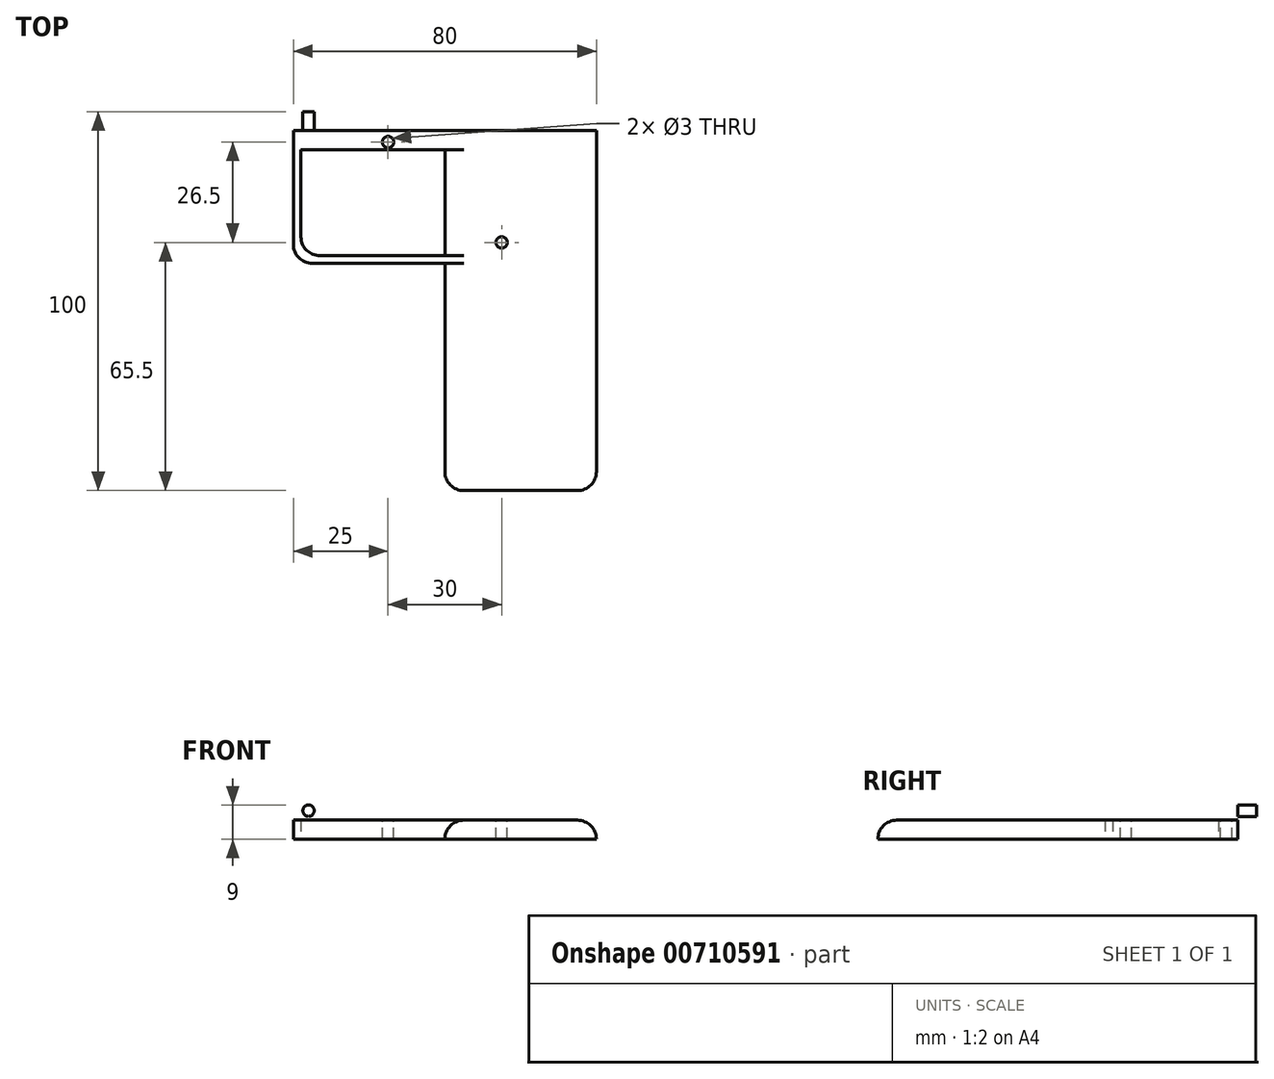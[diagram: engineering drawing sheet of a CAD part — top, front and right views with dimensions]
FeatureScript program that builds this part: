
annotation { "Feature Type Name" : "Feature", "Feature Type Description" : "" }
export const myFeature = defineFeature(function(context is Context, id is Id, definition is map)
    precondition{}
    {
        {
            var Q0;
            Q0=qCreatedBy(makeId("Top.planeOp"),FACE);
            var sketch = newSketch(context, id + "F0", { "sketchPlane" : qUnion([Q0])});
            skLineSegment(sketch, "E0.bottom", {"start": v(20, 50) * mm, "end": v(-20, 50) * mm});
            skLineSegment(sketch, "E0.top", {"start": v(20, -50) * mm, "end": v(-20, -50) * mm});
            skLineSegment(sketch, "E0.left", {"start": v(20, 50) * mm, "end": v(20, -50) * mm});
            skLineSegment(sketch, "E0.right", {"start": v(-20, 50) * mm, "end": v(-20, -50) * mm});
            skPoint(sketch, "E0.middle", {"position": v(0, 0) * mm});
            skLineSegment(sketch, "E1.bottom", {"start": v(-20, 50) * mm, "end": v(-60, 50) * mm});
            skLineSegment(sketch, "E1.top", {"start": v(-20, 10) * mm, "end": v(-60, 10) * mm});
            skLineSegment(sketch, "E1.left", {"start": v(-20, 50) * mm, "end": v(-20, 10) * mm});
            skLineSegment(sketch, "E1.right", {"start": v(-60, 50) * mm, "end": v(-60, 10) * mm});
            skLineSegment(sketch, "E2", {"start": v(-60, 50) * mm, "end": v(-58, 50) * mm});
            skLineSegment(sketch, "E3", {"start": v(-58, 50) * mm, "end": v(-58, 40) * mm});
            skLineSegment(sketch, "E4", {"start": v(-20, 10) * mm, "end": v(-20, 12) * mm});
            skLineSegment(sketch, "E5.bottom", {"start": v(-20, 12) * mm, "end": v(-58, 12) * mm});
            skLineSegment(sketch, "E5.top", {"start": v(-20, 40) * mm, "end": v(-58, 40) * mm});
            skLineSegment(sketch, "E5.left", {"start": v(-20, 12) * mm, "end": v(-20, 40) * mm});
            skLineSegment(sketch, "E5.right", {"start": v(-58, 12) * mm, "end": v(-58, 40) * mm});
            skSolve(sketch);
        }
        {
            var Q0;
            Q0=makeQuery(id+"F0.imprint","IMPRINT",FACE,{"disambiguationData":[TD([[makeQuery(id+"F0.imprint","IMPRINT",EDGE,{"derivedFrom":sQuery(id+"F0.wireOp",EDGE,"E0.bottom")}),1.0]])]});
            var Q1;
            Q1=makeQuery(id+"F0.imprint","IMPRINT",FACE,{"disambiguationData":[TD([[makeQuery(id+"F0.imprint","IMPRINT",EDGE,{"derivedFrom":sQuery(id+"F0.wireOp",EDGE,"E1.bottom")}),1.0]])]});
            var Q2;
            Q2=makeQuery(id+"F0.imprint","IMPRINT",FACE,{"disambiguationData":[TD([[makeQuery(id+"F0.imprint","IMPRINT",EDGE,{"derivedFrom":sQuery(id+"F0.wireOp",EDGE,"E1.top")}),-1.0]])]});
            extrude(context, id + "F1", {"entities" : qUnion([Q0, Q1, Q2]), "depth" : 5 * mm, "offsetDistance" : 25 * mm});
        }
        {
            var Q0;
            Q0=makeQuery(id+"F1.opExtrude","CAP_FACE",FACE,{"disambiguationData":[OSD([sQuery(id+"F0.wireOp",EDGE,"E0.bottom"),sQuery(id+"F0.wireOp",EDGE,"E0.top"),sQuery(id+"F0.wireOp",EDGE,"E0.left"),sQuery(id+"F0.wireOp",EDGE,"E0.right"),sQuery(id+"F0.wireOp",EDGE,"E1.bottom"),sQuery(id+"F0.wireOp",EDGE,"E1.top"),sQuery(id+"F0.wireOp",EDGE,"E1.right"),sQuery(id+"F0.wireOp",EDGE,"E2"),sQuery(id+"F0.wireOp",EDGE,"E5.bottom"),sQuery(id+"F0.wireOp",EDGE,"E5.top"),sQuery(id+"F0.wireOp",EDGE,"E5.left"),sQuery(id+"F0.wireOp",EDGE,"E5.right")])],"isStart":false});
            var sketch = newSketch(context, id + "F2", { "sketchPlane" : qUnion([Q0])});
            skLineSegment(sketch, "E6", {"start": v(-20, 40) * mm, "end": v(-35, 40) * mm, "construction": true});
            skLineSegment(sketch, "E7", {"start": v(-35, 40) * mm, "end": v(-35, 42) * mm, "construction": true});
            skCircle(sketch, "E8", {"center": v(-35, 42) * mm, "radius": 1.5 * mm});
            skLineSegment(sketch, "E9", {"start": v(-35, 42) * mm, "end": v(-35, 18.5) * mm, "construction": true});
            skLineSegment(sketch, "E10", {"start": v(-35, 18.5) * mm, "end": v(-5, 18.5) * mm, "construction": true});
            skLineSegment(sketch, "E11", {"start": v(-5, 18.5) * mm, "end": v(-5, 15.5) * mm, "construction": true});
            skCircle(sketch, "E12", {"center": v(-5, 15.5) * mm, "radius": 1.5 * mm});
            skSolve(sketch);
        }
        {
            var Q0;
            Q0=makeQuery(id+"F2.imprint","IMPRINT",FACE,{"disambiguationData":[TD([[makeQuery(id+"F2.imprint","IMPRINT",EDGE,{"derivedFrom":sQuery(id+"F2.wireOp",EDGE,"E8")}),1.0]])]});
            var Q1;
            Q1=makeQuery(id+"F2.imprint","IMPRINT",FACE,{"disambiguationData":[TD([[makeQuery(id+"F2.imprint","IMPRINT",EDGE,{"derivedFrom":sQuery(id+"F2.wireOp",EDGE,"E12")}),1.0]])]});
            var Q2;
            Q2=makeQuery(id+"F2.imprint","IMPRINT",FACE,{"disambiguationData":[TD([[makeQuery(id+"F2.imprint","IMPRINT",EDGE,{"derivedFrom":sQuery(id+"F2.wireOp",EDGE,"vCmjWVmu-7WJX-9hG4-9sAc-bVtIOR9l7AIR")}),1.0]])]});
            extrude(context, id + "F3", {"entities" : qUnion([Q0, Q1, Q2]), "operationType" : NewBodyOperationType.REMOVE, "oppositeDirection" : true, "depth" : 5 * mm, "offsetDistance" : 25 * mm});
        }
        {
            var Q0;
            Q0=makeQuery(id+"F1.opExtrude","CAP_FACE",FACE,{"disambiguationData":[OSD([sQuery(id+"F0.wireOp",EDGE,"E0.bottom"),sQuery(id+"F0.wireOp",EDGE,"E0.top"),sQuery(id+"F0.wireOp",EDGE,"E0.left"),sQuery(id+"F0.wireOp",EDGE,"E0.right"),sQuery(id+"F0.wireOp",EDGE,"E1.bottom"),sQuery(id+"F0.wireOp",EDGE,"E1.top"),sQuery(id+"F0.wireOp",EDGE,"E1.right"),sQuery(id+"F0.wireOp",EDGE,"E2"),sQuery(id+"F0.wireOp",EDGE,"E5.bottom"),sQuery(id+"F0.wireOp",EDGE,"E5.top"),sQuery(id+"F0.wireOp",EDGE,"E5.left"),sQuery(id+"F0.wireOp",EDGE,"E5.right")])],"isStart":false});
            var sketch = newSketch(context, id + "F4", { "sketchPlane" : qUnion([Q0])});
            skLineSegment(sketch, "E13", {"start": v(20, 50) * mm, "end": v(12, 50) * mm});
            skLineSegment(sketch, "E14", {"start": v(12, 50) * mm, "end": v(12, 45) * mm});
            skLineSegment(sketch, "E15", {"start": v(12, 45) * mm, "end": v(20, 45) * mm});
            skLineSegment(sketch, "E16.MirrorCS", {"start": v(-52, 50) * mm, "end": v(-52, 45) * mm});
            skLineSegment(sketch, "E17.MirrorCS", {"start": v(-52, 45) * mm, "end": v(-60, 45) * mm});
            skSolve(sketch);
        }
        {
            var Q0;
            {var subQ0=sQuery(id+"F4.wireOp",EDGE,"E13");Q0=makeQuery(id+"F4.imprint","IMPRINT",FACE,{"disambiguationData":[TD([[makeQuery(id+"F4.imprint","IMPRINT",EDGE,{"derivedFrom":subQ0}),1.0]])]});}
            var Q1;
            {var subQ0=sQuery(id+"F4.wireOp",EDGE,"E16.MirrorCS");Q1=makeQuery(id+"F4.imprint","IMPRINT",FACE,{"disambiguationData":[TD([[makeQuery(id+"F4.imprint","IMPRINT",EDGE,{"derivedFrom":subQ0}),-1.0]])]});}
            extrude(context, id + "F5", {"entities" : qUnion([Q0, Q1]), "operationType" : NewBodyOperationType.ADD, "depth" : 5 * mm, "offsetDistance" : 25 * mm});
        }
        {
            var Q0;
            Q0=makeQuery(id+"F5.boolean.opBoolean","MERGE",FACE,{"derivedFrom":[makeQuery(id+"F1.opExtrude","SWEPT_FACE",FACE,{"disambiguationData":[OSD([sQuery(id+"F0.wireOp",EDGE,"E0.bottom"),sQuery(id+"F0.wireOp",EDGE,"E1.bottom"),sQuery(id+"F0.wireOp",EDGE,"E2")])]}),makeQuery(id+"F5.opExtrude","SWEPT_FACE",FACE,{"disambiguationData":[OSD([sQuery(id+"F4.wireOp",EDGE,"E13")])]})]});
            var sketch = newSketch(context, id + "F6", { "sketchPlane" : qUnion([Q0])});
            skLineSegment(sketch, "E18", {"start": v(-20, 10) * mm, "end": v(-16, 10) * mm});
            skLineSegment(sketch, "E19", {"start": v(-16, 10) * mm, "end": v(-16, 7.5) * mm});
            skCircle(sketch, "E20", {"center": v(-16, 7.5) * mm, "radius": 1.5 * mm});
            skLineSegment(sketch, "E21", {"start": v(20, 0) * mm, "end": v(20, 5) * mm, "construction": true});
            skCircle(sketch, "E22.MirrorC", {"center": v(56, 7.5) * mm, "radius": 1.5 * mm});
            skSolve(sketch);
        }
        {
            var Q0;
            Q0=makeQuery(id+"F6.imprint","IMPRINT",FACE,{"disambiguationData":[TD([[makeQuery(id+"F6.imprint","IMPRINT",EDGE,{"derivedFrom":sQuery(id+"F6.wireOp",EDGE,"E20")}),1.0]])]});
            var Q1;
            Q1=makeQuery(id+"F6.imprint","IMPRINT",FACE,{"disambiguationData":[TD([[makeQuery(id+"F6.imprint","IMPRINT",EDGE,{"derivedFrom":sQuery(id+"F6.wireOp",EDGE,"E22.MirrorC")}),-1.0]])]});
            extrude(context, id + "F7", {"entities" : qUnion([Q0, Q1]), "operationType" : NewBodyOperationType.REMOVE, "oppositeDirection" : true, "depth" : 5 * mm, "offsetDistance" : 25 * mm});
        }
        {
            var Q0;
            Q0=makeQuery(id+"F1.opExtrude","SWEPT_EDGE",EDGE,{"disambiguationData":[OSD([sQuery(id+"F0.wireOp",EDGE,"E1.top"),sQuery(id+"F0.wireOp",EDGE,"E1.right")])]});
            var Q1;
            Q1=makeQuery(id+"F1.opExtrude","SWEPT_EDGE",EDGE,{"disambiguationData":[OSD([sQuery(id+"F0.wireOp",EDGE,"E5.bottom"),sQuery(id+"F0.wireOp",EDGE,"E5.right")])]});
            var Q2;
            Q2=makeQuery(id+"F1.opExtrude","CAP_EDGE",EDGE,{"disambiguationData":[OSD([sQuery(id+"F0.wireOp",EDGE,"E0.right")])],"isStart":false});
            var Q3;
            Q3=makeQuery(id+"F1.opExtrude","CAP_EDGE",EDGE,{"disambiguationData":[OSD([sQuery(id+"F0.wireOp",EDGE,"E5.left")])],"isStart":false});
            var Q4;
            Q4=makeQuery(id+"F1.opExtrude","CAP_EDGE",EDGE,{"disambiguationData":[OSD([sQuery(id+"F0.wireOp",EDGE,"E0.top")])],"isStart":false});
            var Q5;
            Q5=makeQuery(id+"F1.opExtrude","CAP_EDGE",EDGE,{"disambiguationData":[OSD([sQuery(id+"F0.wireOp",EDGE,"E0.left")])],"isStart":false});
            var Q6;
            Q6=makeQuery(id+"F1.opExtrude","SWEPT_EDGE",EDGE,{"disambiguationData":[OSD([sQuery(id+"F0.wireOp",EDGE,"E0.top"),sQuery(id+"F0.wireOp",EDGE,"E0.right")])]});
            var Q7;
            Q7=makeQuery(id+"F1.opExtrude","SWEPT_EDGE",EDGE,{"disambiguationData":[OSD([sQuery(id+"F0.wireOp",EDGE,"E0.top"),sQuery(id+"F0.wireOp",EDGE,"E0.left")])]});
            fillet(context, id + "F8", {"entities" : qUnion([Q0, Q1, Q2, Q3, Q4, Q5, Q6, Q7]), "radius" : 5 * mm, "tangentPropagation" : true, "allowEdgeOverflow" : false});
        }
    });
